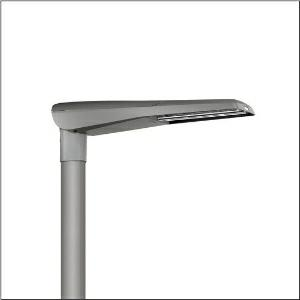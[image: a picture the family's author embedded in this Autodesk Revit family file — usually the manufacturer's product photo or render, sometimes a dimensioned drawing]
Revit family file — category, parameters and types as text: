
# Revit family: streetlight_sl_11_iq_mini___st0_5st0_5_5xc2hc1f08ge_9336
name_source: partatom
category: Lighting Fixtures
units: mm (PartAtom-declared; Revit-internal decimal feet)

## family parameters
Cut with Voids When Loaded = No
Host = Face
Light Source = No
Part Type = Normal
Room Calculation Point = No
Round Connector Dimension = Use Diameter
Shared = No

## types (1)
- --- (1 x LED, 3020 lm, 25.3 W, 2200K)
    Apparent Load = 25 VA
    CIE Flux Codes = 43 74 97 100 100
    Color Rendering = 70
    Color Temperature = 2200K
    Default Elevation = 1800 mm
    Description = Streetlight SL 11 iQ mini, mast luminaire, primary light control with 3 zone facetted reflector, of plastic, silver coated, highly specular, primary optical cover: cover, of PMMA, transparent, light distribution: ST0.5ST0.5, light emission: direct distribution, primary light characteristic: asymmetric, installation type: post-top, side-entry, lamps: LED, High Power LED, rated values: 3.550lm | 24,9W | 142,6lm/W (begin service life); end service life: 3.550lm | 25,7W; at 50% lumin. flux: 1.775lm | 12,8W | 138,7lm/W, colour temperature: 2200/2700/3000/4000K, colour rendering: CRI > 70, light colour: 722/727/730/740, light setting 1 begin service life: 100% | 3.550lm | 24,9W | 142,6lm/W | 3.000K, light setting 1 end service life: 25,7W, further light settings possible, control: Street-Remote, Auto-Match, Temp-Guard, Lumen-Switch, Night-Set, Smart-Wire, Light-Fading, Desk-Remote (wireless, voltage-free reading and setting of iQ features in the workshop via application-optimized NFC function/RFID function), optimised constant luminous flux control (CLO 2.0), with cable H07RN-F 3x 1.5mm², mains connection: 230..240V, AC, 50/60Hz, connection cable pre-assembled, cable length: 6,5m, luminaire housing, of diecast aluminium, powder-coated, SITECO metallic grey (DB 702S), please order mast flange separately, inclination adjustable without tools: 0°, 5°, 10°, 15° (post-top) | 0°, -5°, -10°, -15° (side-entry), sealing non-destructively replaceable, multi-level sealing system, length: 736mm, width: 174mm, height: 116mm, mast flange for spigot size: 42mm (side-entry): 5XC10008XM4, 60/48mm (side-entry/post-top): 5XC10108XM2, 76/60mm (side-entry/post-top): 5XC10108XM1, equipment: standard, protection rating (complete): IP66, insulation class (complete): insulation class II (safety insulation), certification: CE, ENEC, ENEC+, VDE, impact resistance: IK10, permissible operating ambient temperature for outdoor applications: -25..+50°C, standard-compliant lighting for roads and squares, Environmental Product Declaration (EPD) tested and certified by an independent institute, packaging unit: 1 piece

Light Distribution: ST0.5ST0.5
    Height = 116 mm
    Lamp = 1 x LED
    Lamp Light Flux = 3020 lm
    Lamp Power = 25.3 W
    Lamp count = 1
    Length = 736 mm
    Luminous efficacy = 119 lm/W
    Manufacturer = Siteco
    ModVariant = No
    Model = 5XC2HC1F08GE
    Number of Poles = 1
    OnlyDefault = Yes
    Power Factor = 1
    Product Name = Streetlight SL 11 iQ mini | ST0.5ST0.5
    Product group = mast luminaire | pylon top
    ProductGroupID = 6100
    Protection Class = Protection class II
    Protection Degree = IP 66
    RLX_Detail_Level = 1
    RLX_Emergency_Light_Flux = 0 lm
    RLX_Emergency_Type = 0
    RLX_Emergency_Type_DB = No
    RlxData = <blob elided: 58117 chars, md5=18784291>
    Socket = socket
    Standby Power = 0 W
    System Light Flux = 3020 lm
    System Power = 25 W
    Type Comments = individual setting: luminous flux: 100 % | dim-lin: 254 | 351 mA
    Type Image = l_1003508.jpg
    URL = http://relux.com
    VarID = @adj_042729
    Voltage = 0 V
    Weight = 0.00 kg
    Width = 174 mm

## geometry (parser evidence)
native form markers: Blend x4, Sweep x8
no freeform markers — native parametric forms only
